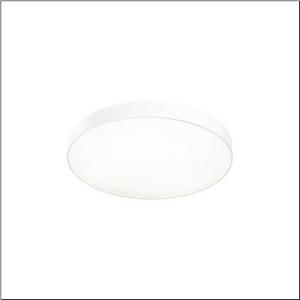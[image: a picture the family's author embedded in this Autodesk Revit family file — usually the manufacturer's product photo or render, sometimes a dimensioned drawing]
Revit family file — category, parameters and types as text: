
# Revit family: round_21_m_51mr36gd0321w
name_source: partatom
category: Lighting Fixtures
units: mm (PartAtom-declared; Revit-internal decimal feet)

## family parameters
Cut with Voids When Loaded = No
Host = Face
Light Source = No
Part Type = Normal
Room Calculation Point = No
Round Connector Dimension = Use Diameter
Shared = No

## types (1)
- Round 21 M (1 x LED, 7550 lm, 54.6 W, 3000K)
    Apparent Load = 55 VA
    CIE Flux Codes = 49 80 96 85 100
    Color Rendering = 80
    Color Temperature = 3000K
    Default Elevation = 1800 mm
    Description = Round 21 M, wall and ceiling luminaire, primary optical cover: cover, of PMMA, opal, light emission: direct/indirect distribution, primary light characteristic: symmetric, installation type: suspended mounting, surface-mounted, LED, rated luminous flux: 7.550lm, luminous efficacy: 138lm/W, light colour: 830, colour temperature: 3000K, control gear: DALI 2, with terminal, 5-pole, mains connection: 230V, AC, 50/60Hz, rated input power: 54.6W, housing, of aluminium, coated, white, diameter: 600mm, height: 62mm, protection rating (complete): IP40, insulation class (complete): insulation class I (protective earthing), certification: CE, impact resistance: IK04, permissible operating ambient temperature: -10..+35°C, packaging unit: 1 piece
    Height = 87 mm
    Lamp = 1 x LED
    Lamp Light Flux = 7550 lm
    Lamp Power = 54.6 W
    Lamp count = 1
    Length = 600 mm
    Luminous efficacy = 138 lm/W
    Manufacturer = Siteco
    ModVariant = No
    Model = 51MR36GD0321W
    Mounting Place = Ceiling
    Mounting Type = Surface mounted
    Number of Poles = 1
    OnlyDefault = Yes
    Power Factor = 1
    Product Name = Round 21 M
    Product group = wall and ceiling luminaire | ceiling mounted
    ProductGroupID = 305
    Protection Class = Protection class I
    Protection Degree = IP 40
    RLX_Detail_Level = 1
    RLX_Emergency_Light_Flux = 0 lm
    RLX_Emergency_Type = 0
    RLX_Emergency_Type_DB = No
    RlxData = <blob elided: 12141 chars, md5=d088b667>
    Socket = socket
    Standby Power = 0 W
    System Light Flux = 7550 lm
    System Power = 55 W
    Type Comments = Product without accessories
    Type Image = l_1258330.jpg
    URL = http://relux.com
    VarID = ---
    Voltage = 0 V
    Weight = 0.00 kg
    Width = 0 mm  [stored 0 ft]

note: [stored X ft] marks values corroborated as IEEE doubles in the binary element streams (Revit-internal decimal feet)

## geometry (parser evidence)
native form markers: Sweep x11
no freeform markers — native parametric forms only
